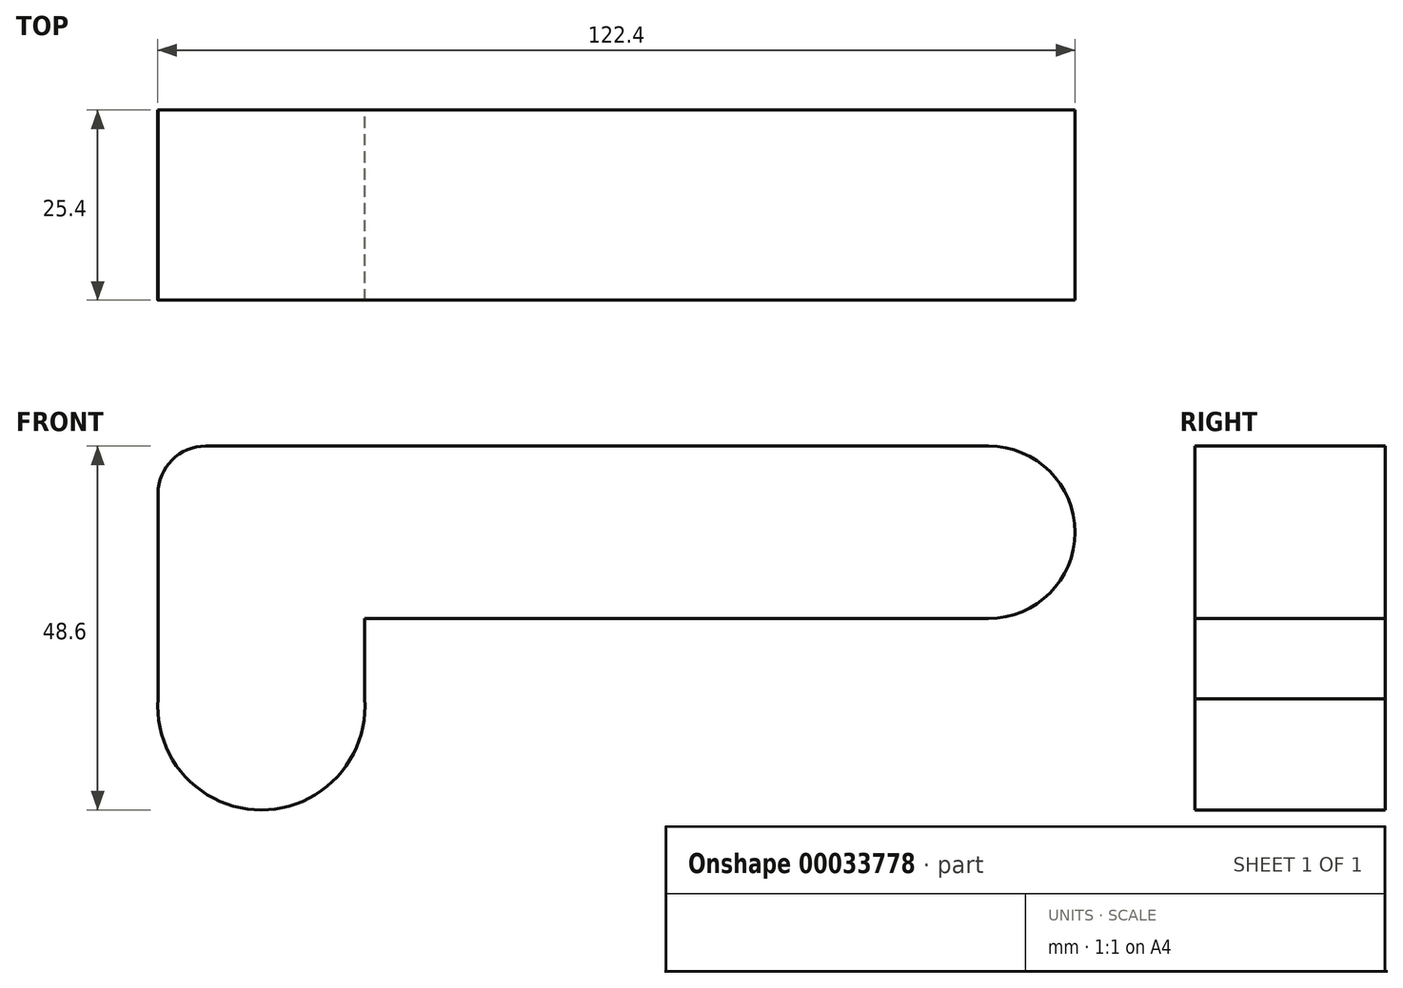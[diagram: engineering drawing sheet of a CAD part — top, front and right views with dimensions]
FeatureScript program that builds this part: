
annotation { "Feature Type Name" : "Feature", "Feature Type Description" : "" }
export const myFeature = defineFeature(function(context is Context, id is Id, definition is map)
    precondition{}
    {
        {
            var Q0;
            Q0=qCreatedBy(makeId("Front.planeOp"),FACE);
            var sketch = newSketch(context, id + "F0", { "sketchPlane" : qUnion([Q0])});
            skLineSegment(sketch, "E0", {"start": v(-52.91, 31.4) * mm, "end": v(51.59, 31.4) * mm});
            skLineSegment(sketch, "E1", {"start": v(51.59, 31.4) * mm, "end": v(51.59, 8.38) * mm});
            skLineSegment(sketch, "E2", {"start": v(51.59, 8.38) * mm, "end": v(-31.7, 8.38) * mm});
            skLineSegment(sketch, "E3", {"start": v(-31.7, 8.38) * mm, "end": v(-31.7, -4.4) * mm});
            skLineSegment(sketch, "E4", {"start": v(-59.26, -4.4) * mm, "end": v(-59.26, 25.05) * mm});
            skArc(sketch, "E5", {"start": v(51.59, 8.38) * mm, "mid": v(63.1, 19.9) * mm, "end": v(51.59, 31.4) * mm});
            skCircle(sketch, "E6", {"center": v(-45.48, -3.38) * mm, "radius": 13.82 * mm});
            skPoint(sketch, "E6.first.point", {"position": v(-45.48, -17.2) * mm});
            skPoint(sketch, "E6.second.point", {"position": v(-31.7, -4.4) * mm});
            skPoint(sketch, "E6.third.point", {"position": v(-59.26, -4.4) * mm});
            skPoint(sketch, "E6.third.point.positionSnap0", {"position": v(-31.7, -4.4) * mm});
            skPoint(sketch, "E7.orphan", {"position": v(-59.26, -17.2) * mm});
            skPoint(sketch, "E8.orphan", {"position": v(-31.7, -17.2) * mm});
            skPoint(sketch, "E9.visualSharp", {"position": v(-59.26, 31.4) * mm});
            skArc(sketch, "E9.filletArc", {"start": v(-52.91, 31.4) * mm, "mid": v(-57.4, 29.54) * mm, "end": v(-59.26, 25.05) * mm});
            skSolve(sketch);
        }
        {
            var Q0;
            Q0 = qSketchRegion(id + "F0", true);
            extrude(context, id + "F1", {"entities" : qUnion([Q0]), "depth" : 25.4 * mm});
        }
    });
